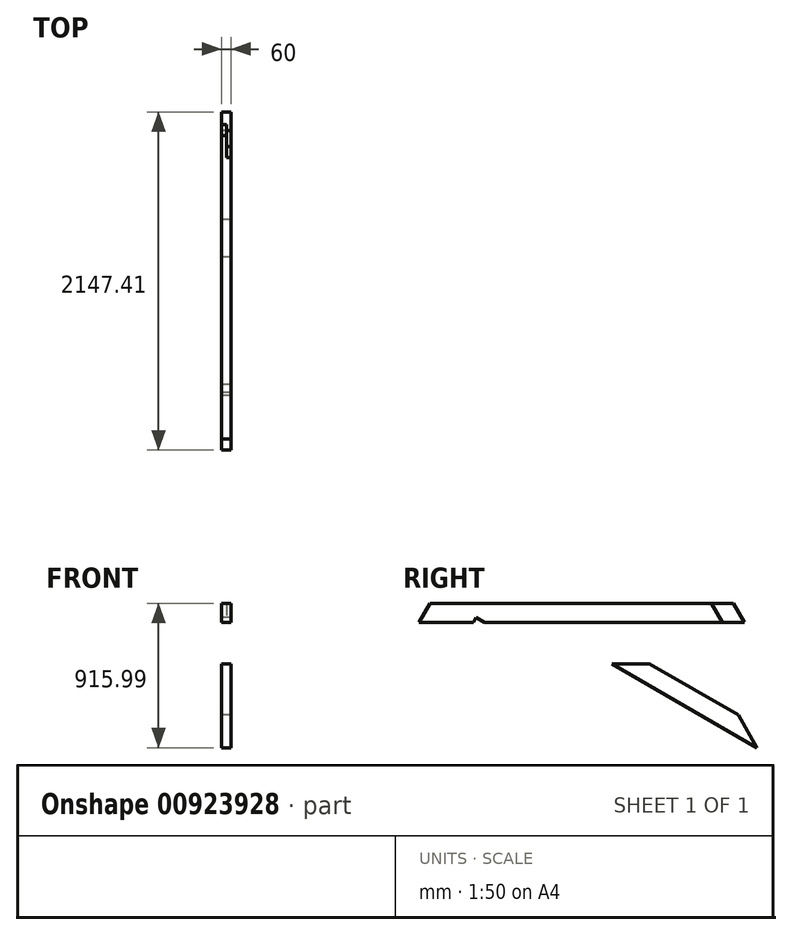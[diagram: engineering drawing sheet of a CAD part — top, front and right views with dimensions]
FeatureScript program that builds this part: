
annotation { "Feature Type Name" : "Feature", "Feature Type Description" : "" }
export const myFeature = defineFeature(function(context is Context, id is Id, definition is map)
    precondition{}
    {
        {
            var Q0;
            Q0=qCreatedBy(makeId("Right.planeOp"),FACE);
            var sketch = newSketch(context, id + "F0", { "sketchPlane" : qUnion([Q0])});
            skLineSegment(sketch, "E0.top", {"start": v(-2646.47, -829.73) * mm, "end": v(-1866.97, -829.73) * mm});
            skLineSegment(sketch, "E1", {"start": v(-215.75, -709.73) * mm, "end": v(-146.47, -829.73) * mm});
            skLineSegment(sketch, "E2", {"start": v(-354.59, -709.73) * mm, "end": v(-215.75, -709.73) * mm});
            skLineSegment(sketch, "E3", {"start": v(-285.3, -829.73) * mm, "end": v(-146.47, -829.73) * mm});
            skLineSegment(sketch, "E4", {"start": v(-354.59, -709.73) * mm, "end": v(-285.3, -829.73) * mm});
            skLineSegment(sketch, "E5.top", {"start": v(895.28, -2874.56) * mm, "end": v(-285.3, -829.73) * mm, "construction": true});
            skLineSegment(sketch, "E6.MirrorCS", {"start": v(999.2, -2814.56) * mm, "end": v(895.28, -2874.56) * mm, "construction": true});
            skLineSegment(sketch, "E7.MirrorCS", {"start": v(-146.74, -829.73) * mm, "end": v(-285.3, -829.73) * mm, "construction": true});
            skLineSegment(sketch, "E8.MirrorCS", {"start": v(999.2, -2814.56) * mm, "end": v(-146.74, -829.73) * mm, "construction": true});
            skLineSegment(sketch, "E9.bottom", {"start": v(-1849.65, -799.73) * mm, "end": v(-663.2, -1484.73) * mm, "construction": true});
            skLineSegment(sketch, "E9.top", {"start": v(-1909.65, -903.65) * mm, "end": v(-723.2, -1588.65) * mm, "construction": true});
            skLineSegment(sketch, "E9.left", {"start": v(-1849.65, -799.73) * mm, "end": v(-1909.65, -903.65) * mm, "construction": true});
            skLineSegment(sketch, "E9.right", {"start": v(523.26, -2169.73) * mm, "end": v(463.26, -2273.65) * mm, "construction": true});
            skLineSegment(sketch, "E10", {"start": v(-663.2, -1484.73) * mm, "end": v(523.26, -2169.73) * mm, "construction": true});
            skLineSegment(sketch, "E11", {"start": v(-723.2, -1588.65) * mm, "end": v(463.26, -2273.65) * mm, "construction": true});
            skLineSegment(sketch, "E12", {"start": v(-1866.97, -829.73) * mm, "end": v(-1849.65, -799.73) * mm});
            skLineSegment(sketch, "E13", {"start": v(-1849.65, -799.73) * mm, "end": v(-1797.69, -829.73) * mm});
            skLineSegment(sketch, "E14", {"start": v(-1797.69, -829.73) * mm, "end": v(-285.3, -829.73) * mm});
            skLineSegment(sketch, "E15", {"start": v(-2213.3, -829.73) * mm, "end": v(-2144.01, -709.73) * mm});
            skLineSegment(sketch, "E16", {"start": v(-2577.18, -709.73) * mm, "end": v(-354.59, -709.73) * mm});
            skLineSegment(sketch, "E17", {"start": v(-663.2, -1484.73) * mm, "end": v(-408.7, -1043.92) * mm, "construction": true});
            skLineSegment(sketch, "E18", {"start": v(-408.7, -1043.92) * mm, "end": v(-779.69, -829.73) * mm, "construction": true});
            skLineSegment(sketch, "E19", {"start": v(-779.69, -829.73) * mm, "end": v(-987.53, -709.73) * mm, "construction": true});
            skLineSegment(sketch, "E20", {"start": v(-1909.65, -903.65) * mm, "end": v(-2309.63, -1596.44) * mm, "construction": true});
            skLineSegment(sketch, "E21", {"start": v(-2309.63, -1596.44) * mm, "end": v(-2569.37, -1446.47) * mm, "construction": true});
            skLineSegment(sketch, "E22", {"start": v(-2569.37, -1446.47) * mm, "end": v(-2213.3, -829.73) * mm, "construction": true});
            skSolve(sketch);
        }
        {
            var Q0;
            Q0=makeQuery(id+"F0.imprint","IMPRINT",FACE,{"disambiguationData":[TD([[makeQuery(id+"F0.imprint","IMPRINT",EDGE,{"derivedFrom":sQuery(id+"F0.wireOp",EDGE,"E0.top")}),1.0]])]});
            extrude(context, id + "F1", {"entities" : qUnion([Q0]), "depth" : 60 * mm, "offsetDistance" : 25 * mm});
        }
        {
            var Q0;
            Q0=makeQuery(id+"F0.imprint","IMPRINT",FACE,{"disambiguationData":[TD([[makeQuery(id+"F0.imprint","IMPRINT",EDGE,{"derivedFrom":sQuery(id+"F0.wireOp",EDGE,"E1")}),-1.0]])]});
            extrude(context, id + "F2", {"entities" : qUnion([Q0]), "operationType" : NewBodyOperationType.ADD, "depth" : 30 * mm, "offsetDistance" : 25 * mm});
        }
        {
            var Q0;
            Q0=qCreatedBy(makeId("Right.planeOp"),FACE);
            var sketch = newSketch(context, id + "F3", { "sketchPlane" : qUnion([Q0])});
            skLineSegment(sketch, "E23", {"start": v(-466.88, -1256.28) * mm, "end": v(-748.42, -1093.73) * mm});
            skLineSegment(sketch, "E24", {"start": v(-526.6, -1359.72) * mm, "end": v(-987.31, -1093.73) * mm});
            skLineSegment(sketch, "E25", {"start": v(-987.31, -1093.73) * mm, "end": v(-748.42, -1093.73) * mm});
            skLineSegment(sketch, "E26.MirrorCS", {"start": v(-466.88, -1256.28) * mm, "end": v(-185.33, -1418.83) * mm});
            skLineSegment(sketch, "E27.MirrorCS", {"start": v(-526.6, -1359.72) * mm, "end": v(-65.89, -1625.72) * mm});
            skLineSegment(sketch, "E28.MirrorCS", {"start": v(-65.89, -1625.72) * mm, "end": v(-185.33, -1418.83) * mm});
            skLineSegment(sketch, "E29", {"start": v(-125.61, -1522.27) * mm, "end": v(-496.7, -1307.92) * mm, "construction": true});
            skLineSegment(sketch, "E30", {"start": v(-496.7, -1307.92) * mm, "end": v(-867.69, -1093.73) * mm, "construction": true});
            skSolve(sketch);
        }
        {
            var Q0;
            Q0=makeQuery(id+"F2.boolean.opBoolean","MERGE",FACE,{"derivedFrom":[makeQuery(id+"F1.opExtrude","SWEPT_FACE",FACE,{"disambiguationData":[OSD([sQuery(id+"F0.wireOp",EDGE,"E14")])]}),makeQuery(id+"F2.opExtrude","SWEPT_FACE",FACE,{"disambiguationData":[OSD([sQuery(id+"F0.wireOp",EDGE,"E3")])]})]});
            var sketch = newSketch(context, id + "F4", { "sketchPlane" : qUnion([Q0])});
            skLineSegment(sketch, "E31", {"start": v(0, 779.69) * mm, "end": v(60, 779.69) * mm, "construction": true});
            skPoint(sketch, "E32.0", {"position": v(0, 779.69) * mm});
            skSolve(sketch);
        }
        {
            var Q0;
            Q0=makeQuery(id+"F3.imprint","IMPRINT",FACE,{"disambiguationData":[TD([[makeQuery(id+"F3.imprint","IMPRINT",EDGE,{"derivedFrom":sQuery(id+"F3.wireOp",EDGE,"E23")}),1.0]])]});
            extrude(context, id + "F5", {"entities" : qUnion([Q0]), "depth" : 60 * mm, "offsetDistance" : 25 * mm});
        }
        {
            var Q0;
            Q0=makeQuery(id+"F5.opExtrude","SWEPT_FACE",FACE,{"disambiguationData":[OSD([sQuery(id+"F3.wireOp",EDGE,"E25")])]});
            var sketch = newSketch(context, id + "F6", { "sketchPlane" : qUnion([Q0])});
            skPoint(sketch, "E33.0", {"position": v(0, -867.87) * mm});
            skLineSegment(sketch, "E34", {"start": v(0, -867.87) * mm, "end": v(60, -867.87) * mm, "construction": true});
            skSolve(sketch);
        }
        {
            var Q0;
            Q0=makeQuery(id+"F5.opExtrude","SWEPT_FACE",FACE,{"disambiguationData":[OSD([sQuery(id+"F3.wireOp",EDGE,"E28.MirrorCS")])]});
            var sketch = newSketch(context, id + "F7", { "sketchPlane" : qUnion([Q0])});
            skLineSegment(sketch, "E35", {"start": v(-60, -1255.52) * mm, "end": v(0, -1255.52) * mm, "construction": true});
            skSolve(sketch);
        }
    });
